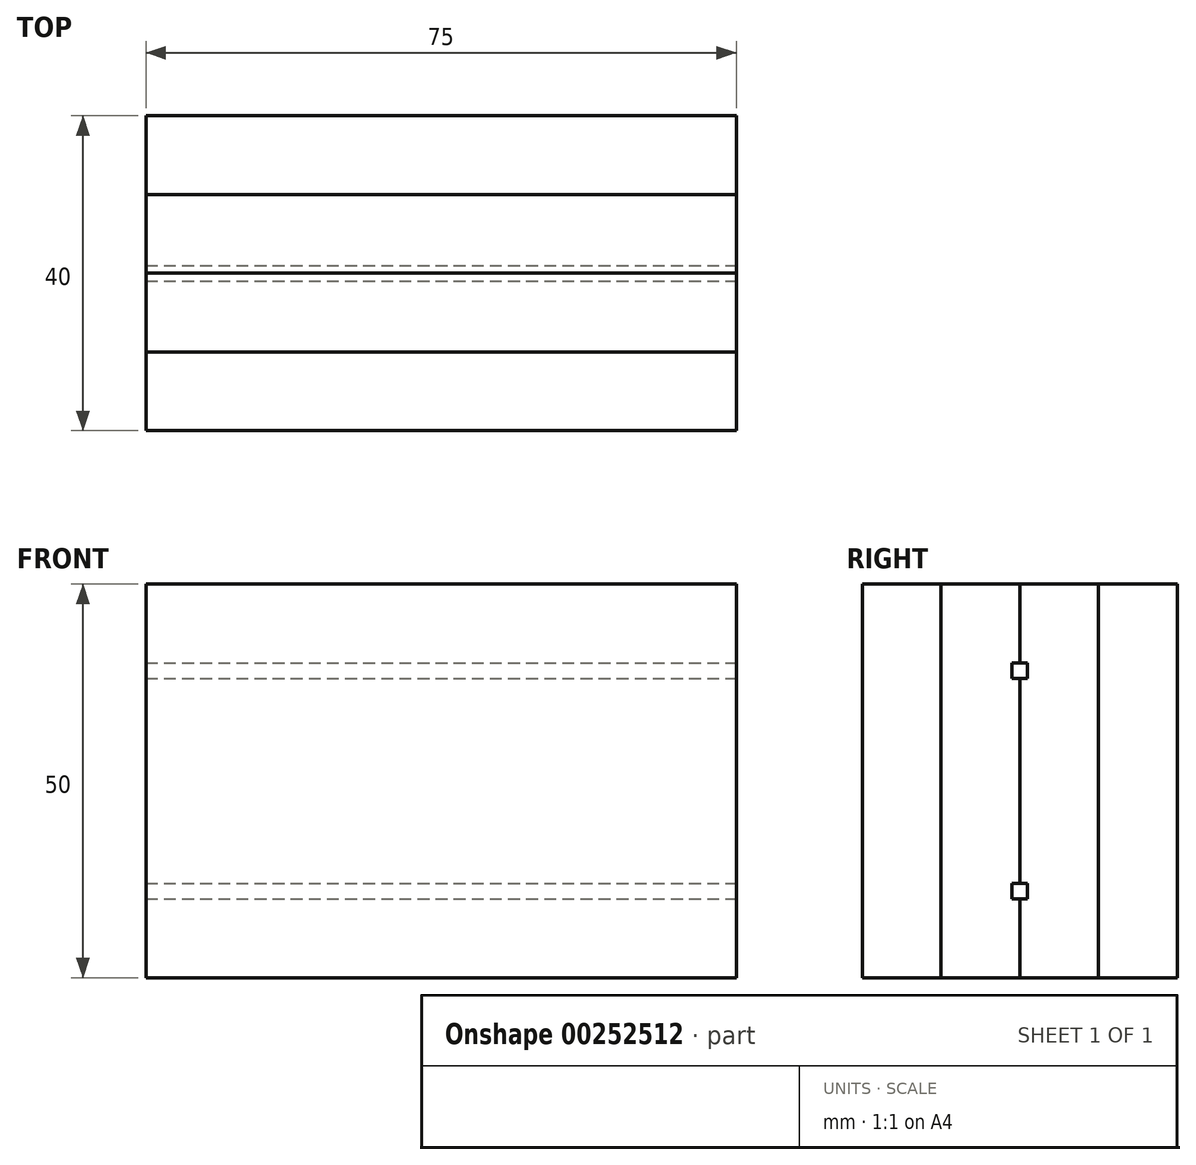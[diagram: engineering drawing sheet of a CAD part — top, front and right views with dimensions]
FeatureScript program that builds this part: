
annotation { "Feature Type Name" : "Feature", "Feature Type Description" : "" }
export const myFeature = defineFeature(function(context is Context, id is Id, definition is map)
    precondition{}
    {
        {
            var Q0;
            Q0=qCreatedBy(makeId("Front.planeOp"),FACE);
            var sketch = newSketch(context, id + "F0", { "sketchPlane" : qUnion([Q0])});
            skLineSegment(sketch, "E0.bottom", {"start": v(37.5, -25) * mm, "end": v(-37.5, -25) * mm});
            skLineSegment(sketch, "E0.top", {"start": v(37.5, 25) * mm, "end": v(-37.5, 25) * mm});
            skLineSegment(sketch, "E0.left", {"start": v(37.5, -25) * mm, "end": v(37.5, 25) * mm});
            skLineSegment(sketch, "E0.right", {"start": v(-37.5, -25) * mm, "end": v(-37.5, 25) * mm});
            skPoint(sketch, "E0.middle", {"position": v(0, 0) * mm});
            skSolve(sketch);
        }
        {
            var Q0;
            Q0 = qSketchRegion(id + "F0", true);
            extrude(context, id + "F1", {"entities" : qUnion([Q0]), "depth" : 10 * mm});
        }
        {
            var Q0;
            Q0=makeQuery(id+"F1.opExtrude","CAP_FACE",FACE,{"disambiguationData":[OSD([sQuery(id+"F0.wireOp",EDGE,"E0.bottom"),sQuery(id+"F0.wireOp",EDGE,"E0.top"),sQuery(id+"F0.wireOp",EDGE,"E0.left"),sQuery(id+"F0.wireOp",EDGE,"E0.right")])],"isStart":false});
            var sketch = newSketch(context, id + "F2", { "sketchPlane" : qUnion([Q0])});
            skLineSegment(sketch, "E1.bottom", {"start": v(37.5, -25) * mm, "end": v(-37.5, -25) * mm});
            skLineSegment(sketch, "E1.top", {"start": v(37.5, 25) * mm, "end": v(-37.5, 25) * mm});
            skLineSegment(sketch, "E1.left", {"start": v(37.5, -25) * mm, "end": v(37.5, 25) * mm});
            skLineSegment(sketch, "E1.right", {"start": v(-37.5, -25) * mm, "end": v(-37.5, 25) * mm});
            skPoint(sketch, "E1.middle", {"position": v(0, 0) * mm});
            skSolve(sketch);
        }
        {
            var Q0;
            Q0 = qSketchRegion(id + "F2", true);
            extrude(context, id + "F3", {"entities" : qUnion([Q0]), "depth" : 10 * mm});
        }
        {
            var Q0;
            Q0=makeQuery(id+"F3.opExtrude","CAP_FACE",FACE,{"disambiguationData":[OSD([sQuery(id+"F2.wireOp",EDGE,"E1.bottom"),sQuery(id+"F2.wireOp",EDGE,"E1.top"),sQuery(id+"F2.wireOp",EDGE,"E1.left"),sQuery(id+"F2.wireOp",EDGE,"E1.right")])],"isStart":false});
            var sketch = newSketch(context, id + "F4", { "sketchPlane" : qUnion([Q0])});
            skLineSegment(sketch, "E2.bottom", {"start": v(-37.5, 15) * mm, "end": v(37.5, 15) * mm});
            skLineSegment(sketch, "E2.top", {"start": v(-37.5, 13) * mm, "end": v(37.5, 13) * mm});
            skLineSegment(sketch, "E2.left", {"start": v(-37.5, 15) * mm, "end": v(-37.5, 13) * mm});
            skLineSegment(sketch, "E2.right", {"start": v(37.5, 15) * mm, "end": v(37.5, 13) * mm});
            skSolve(sketch);
        }
        {
            var Q0;
            Q0 = qSketchRegion(id + "F4", true);
            extrude(context, id + "F5", {"entities" : qUnion([Q0]), "operationType" : NewBodyOperationType.REMOVE, "oppositeDirection" : true, "depth" : 1 * mm});
        }
        {
            var Q0;
            {var subQ0=sQuery(id+"F2.wireOp",EDGE,"E1.bottom");var subQ1=sQuery(id+"F2.wireOp",EDGE,"E1.left");var subQ2=sQuery(id+"F2.wireOp",EDGE,"E1.right");Q0=makeQuery(id+"F5.boolean.opBoolean","SPLIT",FACE,{"disambiguationData":[TD([makeQuery(id+"F3.opExtrude","SWEPT_FACE",FACE,{"disambiguationData":[OSD([subQ0])]})])],"derivedFrom":makeQuery(id+"F3.opExtrude","CAP_FACE",FACE,{"disambiguationData":[OSD([subQ0,sQuery(id+"F2.wireOp",EDGE,"E1.top"),subQ1,subQ2])],"isStart":false})});}
            var sketch = newSketch(context, id + "F6", { "sketchPlane" : qUnion([Q0])});
            skLineSegment(sketch, "E3.bottom", {"start": v(-37.5, -13) * mm, "end": v(37.5, -13) * mm});
            skLineSegment(sketch, "E3.top", {"start": v(-37.5, -15) * mm, "end": v(37.5, -15) * mm});
            skLineSegment(sketch, "E3.left", {"start": v(-37.5, -13) * mm, "end": v(-37.5, -15) * mm});
            skLineSegment(sketch, "E3.right", {"start": v(37.5, -13) * mm, "end": v(37.5, -15) * mm});
            skSolve(sketch);
        }
        {
            var Q0;
            Q0 = qSketchRegion(id + "F6", true);
            extrude(context, id + "F7", {"entities" : qUnion([Q0]), "operationType" : NewBodyOperationType.REMOVE, "oppositeDirection" : true, "depth" : 1 * mm});
        }
        {
            var Q0;
            Q0=makeQuery(id+"F5.boolean.opBoolean","COPY",FACE,{"derivedFrom":makeQuery(id+"F5.opExtrude","CAP_FACE",FACE,{"disambiguationData":[OSD([sQuery(id+"F4.wireOp",EDGE,"E2.bottom"),sQuery(id+"F4.wireOp",EDGE,"E2.top"),sQuery(id+"F4.wireOp",EDGE,"E2.left"),sQuery(id+"F4.wireOp",EDGE,"E2.right")])],"isStart":false})});
            var sketch = newSketch(context, id + "F8", { "sketchPlane" : qUnion([Q0])});
            skLineSegment(sketch, "E4.bottom", {"start": v(-37.5, 15) * mm, "end": v(37.5, 15) * mm});
            skLineSegment(sketch, "E4.top", {"start": v(-37.5, 13) * mm, "end": v(37.5, 13) * mm});
            skLineSegment(sketch, "E4.left", {"start": v(-37.5, 15) * mm, "end": v(-37.5, 13) * mm});
            skLineSegment(sketch, "E4.right", {"start": v(37.5, 15) * mm, "end": v(37.5, 13) * mm});
            skSolve(sketch);
        }
        {
            var Q0;
            Q0 = qSketchRegion(id + "F8", true);
            extrude(context, id + "F9", {"entities" : qUnion([Q0]), "depth" : 2 * mm});
        }
        {
            var Q0;
            Q0=makeQuery(id+"F9.opExtrude","SWEPT_BODY",BODY,{"disambiguationData":[OSD([sQuery(id+"F8.wireOp",EDGE,"E4.bottom"),sQuery(id+"F8.wireOp",EDGE,"E4.top"),sQuery(id+"F8.wireOp",EDGE,"E4.left"),sQuery(id+"F8.wireOp",EDGE,"E4.right")])]});
            transform(context, id + "F10", {"entities" : qUnion([Q0]), "transformType" : TransformType.TRANSLATION_3D, "dx" : 0 * mm, "dy" : 0 * mm, "dz" : -28 * mm, "makeCopy" : true});
        }
        {
            var Q0;
            Q0=makeQuery(id+"F3.opExtrude","SWEPT_BODY",BODY,{"disambiguationData":[OSD([sQuery(id+"F2.wireOp",EDGE,"E1.bottom"),sQuery(id+"F2.wireOp",EDGE,"E1.top"),sQuery(id+"F2.wireOp",EDGE,"E1.left"),sQuery(id+"F2.wireOp",EDGE,"E1.right")])]});
            transform(context, id + "F11", {"entities" : qUnion([Q0]), "transformType" : TransformType.TRANSLATION_3D, "dx" : 0 * mm, "dy" : -10 * mm, "dz" : 0 * mm, "makeCopy" : true});
        }
        {
            var Q0;
            Q0=makeQuery(id+"F11.opPattern","COPY",BODY,{"derivedFrom":makeQuery(id+"F3.opExtrude","SWEPT_BODY",BODY,{"disambiguationData":[OSD([sQuery(id+"F2.wireOp",EDGE,"E1.bottom"),sQuery(id+"F2.wireOp",EDGE,"E1.top"),sQuery(id+"F2.wireOp",EDGE,"E1.left"),sQuery(id+"F2.wireOp",EDGE,"E1.right")])]}),"instanceName":"1"});
            var Q1;
            Q1=makeQuery(id+"F11.opPattern","COPY",EDGE,{"derivedFrom":makeQuery(id+"F3.opExtrude","CAP_EDGE",EDGE,{"disambiguationData":[OSD([sQuery(id+"F2.wireOp",EDGE,"E1.right")])],"isStart":true}),"instanceName":"1"});
            transform(context, id + "F12", {"entities" : qUnion([Q0]), "transformType" : TransformType.ROTATION, "transformAxis" : qUnion([Q1]), "angle" : 180 * degree, "makeCopy" : false});
        }
        {
            var Q0;
            Q0=makeQuery(id+"F11.opPattern","COPY",BODY,{"derivedFrom":makeQuery(id+"F3.opExtrude","SWEPT_BODY",BODY,{"disambiguationData":[OSD([sQuery(id+"F2.wireOp",EDGE,"E1.bottom"),sQuery(id+"F2.wireOp",EDGE,"E1.top"),sQuery(id+"F2.wireOp",EDGE,"E1.left"),sQuery(id+"F2.wireOp",EDGE,"E1.right")])]}),"instanceName":"1"});
            transform(context, id + "F13", {"entities" : qUnion([Q0]), "transformType" : TransformType.TRANSLATION_3D, "dx" : 75 * mm, "dy" : -10 * mm, "dz" : 0 * mm, "makeCopy" : false});
        }
        {
            var Q0;
            Q0=makeQuery(id+"F9.opExtrude","SWEPT_BODY",BODY,{"disambiguationData":[OSD([sQuery(id+"F8.wireOp",EDGE,"E4.bottom"),sQuery(id+"F8.wireOp",EDGE,"E4.top"),sQuery(id+"F8.wireOp",EDGE,"E4.left"),sQuery(id+"F8.wireOp",EDGE,"E4.right")])]});
            transform(context, id + "F14", {"entities" : qUnion([Q0]), "transformType" : TransformType.TRANSLATION_3D, "dx" : 0 * mm, "dy" : -2 * mm, "dz" : 0 * mm, "makeCopy" : true});
        }
        {
            var Q0;
            Q0=makeQuery(id+"F10.opPattern","COPY",BODY,{"derivedFrom":makeQuery(id+"F9.opExtrude","SWEPT_BODY",BODY,{"disambiguationData":[OSD([sQuery(id+"F8.wireOp",EDGE,"E4.bottom"),sQuery(id+"F8.wireOp",EDGE,"E4.top"),sQuery(id+"F8.wireOp",EDGE,"E4.left"),sQuery(id+"F8.wireOp",EDGE,"E4.right")])]}),"instanceName":"1"});
            transform(context, id + "F15", {"entities" : qUnion([Q0]), "transformType" : TransformType.TRANSLATION_3D, "dx" : 0 * mm, "dy" : -2 * mm, "dz" : 0 * mm, "makeCopy" : true});
        }
        {
            var Q0;
            Q0=makeQuery(id+"F1.opExtrude","SWEPT_BODY",BODY,{"disambiguationData":[OSD([sQuery(id+"F0.wireOp",EDGE,"E0.bottom"),sQuery(id+"F0.wireOp",EDGE,"E0.top"),sQuery(id+"F0.wireOp",EDGE,"E0.left"),sQuery(id+"F0.wireOp",EDGE,"E0.right")])]});
            transform(context, id + "F16", {"entities" : qUnion([Q0]), "transformType" : TransformType.TRANSLATION_3D, "dx" : 0 * mm, "dy" : -30 * mm, "dz" : 0 * mm, "makeCopy" : true});
        }
        {
            var Q0;
            Q0=makeQuery(id+"F14.opPattern","COPY",BODY,{"derivedFrom":makeQuery(id+"F9.opExtrude","SWEPT_BODY",BODY,{"disambiguationData":[OSD([sQuery(id+"F8.wireOp",EDGE,"E4.bottom"),sQuery(id+"F8.wireOp",EDGE,"E4.top"),sQuery(id+"F8.wireOp",EDGE,"E4.left"),sQuery(id+"F8.wireOp",EDGE,"E4.right")])]}),"instanceName":"1"});
            deleteBodies(context, id + "F17", {"entities" : qUnion([Q0])});
        }
        {
            var Q0;
            Q0=makeQuery(id+"F15.opPattern","COPY",BODY,{"derivedFrom":makeQuery(id+"F10.opPattern","COPY",BODY,{"derivedFrom":makeQuery(id+"F9.opExtrude","SWEPT_BODY",BODY,{"disambiguationData":[OSD([sQuery(id+"F8.wireOp",EDGE,"E4.bottom"),sQuery(id+"F8.wireOp",EDGE,"E4.top"),sQuery(id+"F8.wireOp",EDGE,"E4.left"),sQuery(id+"F8.wireOp",EDGE,"E4.right")])]}),"instanceName":"1"}),"instanceName":"1"});
            deleteBodies(context, id + "F18", {"entities" : qUnion([Q0])});
        }
        {
            var Q0;
            Q0=makeQuery(id+"F9.opExtrude","SWEPT_BODY",BODY,{"disambiguationData":[OSD([sQuery(id+"F8.wireOp",EDGE,"E4.bottom"),sQuery(id+"F8.wireOp",EDGE,"E4.top"),sQuery(id+"F8.wireOp",EDGE,"E4.left"),sQuery(id+"F8.wireOp",EDGE,"E4.right")])]});
            transform(context, id + "F19", {"entities" : qUnion([Q0]), "transformType" : TransformType.TRANSLATION_3D, "dx" : 0 * mm, "dy" : 0 * mm, "dz" : 0 * mm, "makeCopy" : false});
        }
        {
            var Q0;
            Q0=makeQuery(id+"F10.opPattern","COPY",BODY,{"derivedFrom":makeQuery(id+"F9.opExtrude","SWEPT_BODY",BODY,{"disambiguationData":[OSD([sQuery(id+"F8.wireOp",EDGE,"E4.bottom"),sQuery(id+"F8.wireOp",EDGE,"E4.top"),sQuery(id+"F8.wireOp",EDGE,"E4.left"),sQuery(id+"F8.wireOp",EDGE,"E4.right")])]}),"instanceName":"1"});
            transform(context, id + "F20", {"entities" : qUnion([Q0]), "transformType" : TransformType.TRANSLATION_3D, "dx" : 0 * mm, "dy" : 0 * mm, "dz" : 0 * mm, "makeCopy" : false});
        }
    });
